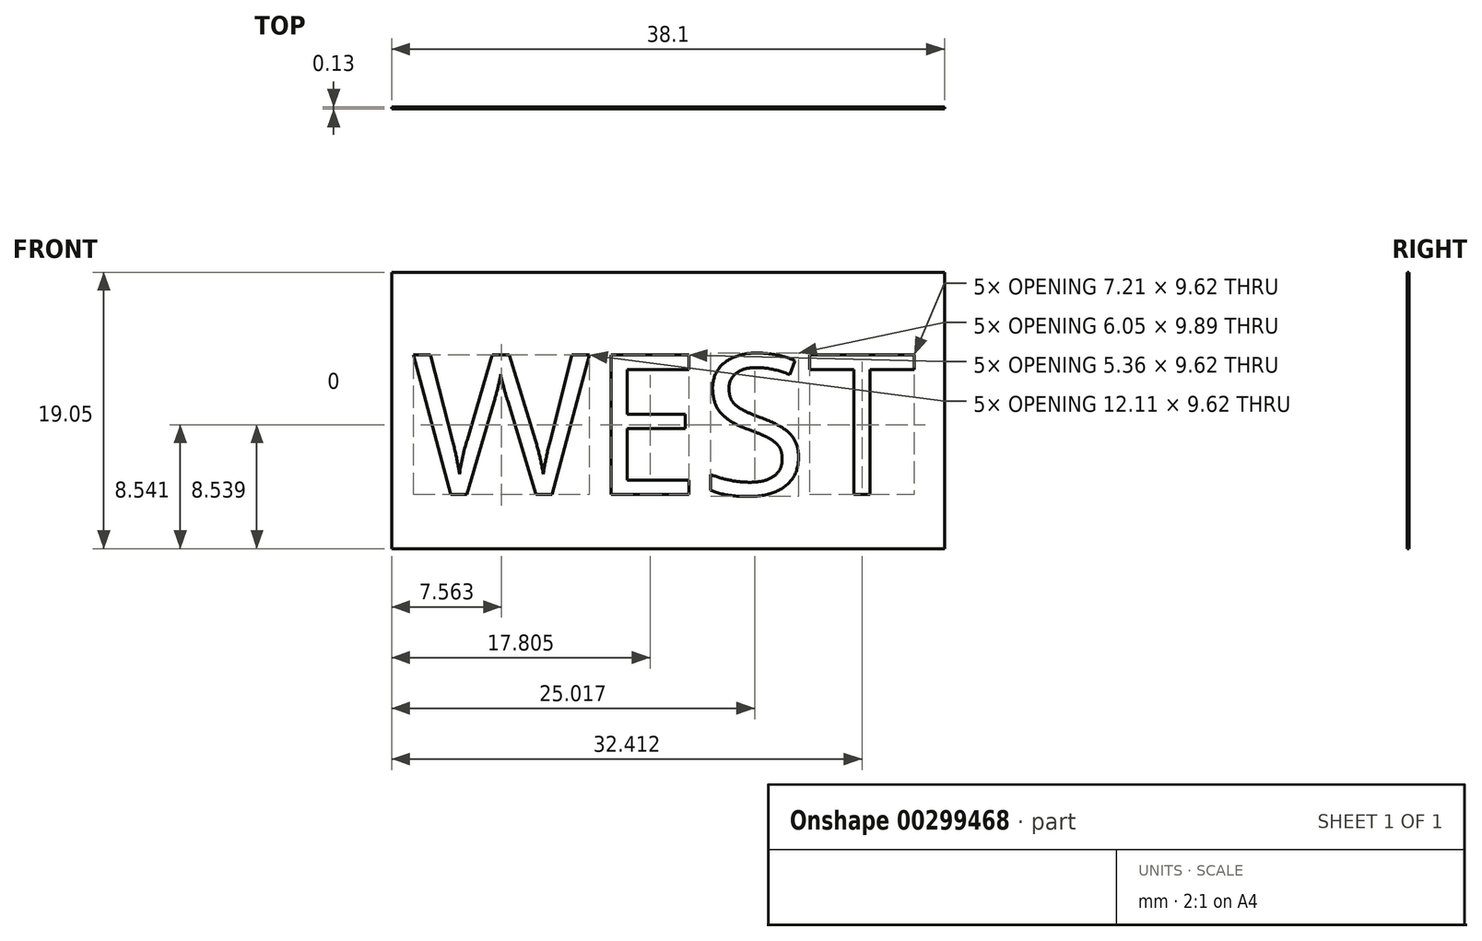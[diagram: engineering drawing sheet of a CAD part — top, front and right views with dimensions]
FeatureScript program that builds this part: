
annotation { "Feature Type Name" : "Feature", "Feature Type Description" : "" }
export const myFeature = defineFeature(function(context is Context, id is Id, definition is map)
    precondition{}
    {
        {
            var Q0;
            Q0=qCreatedBy(makeId("Front.planeOp"),FACE);
            var sketch = newSketch(context, id + "F0", { "sketchPlane" : qUnion([Q0])});
            skLineSegment(sketch, "E0.bottom", {"start": v(0, 0) * mm, "end": v(38.1, 0) * mm});
            skLineSegment(sketch, "E0.top", {"start": v(0, 19.05) * mm, "end": v(38.1, 19.05) * mm});
            skLineSegment(sketch, "E0.left", {"start": v(0, 0) * mm, "end": v(0, 19.05) * mm});
            skLineSegment(sketch, "E0.right", {"start": v(38.1, 0) * mm, "end": v(38.1, 19.05) * mm});
            skSolve(sketch);
        }
        {
            var Q0;
            Q0=makeQuery(id+"F0.imprint","IMPRINT",FACE,{"disambiguationData":[TD([[makeQuery(id+"F0.imprint","IMPRINT",EDGE,{"derivedFrom":sQuery(id+"F0.wireOp",EDGE,"E0.bottom")}),1.0]])]});
            extrude(context, id + "F1", {"entities" : qUnion([Q0]), "depth" : 0.13 * mm});
        }
        {
            var Q0;
            Q0=makeQuery(id+"F1.opExtrude","CAP_FACE",FACE,{"disambiguationData":[OSD([sQuery(id+"F0.wireOp",EDGE,"E0.bottom"),sQuery(id+"F0.wireOp",EDGE,"E0.top"),sQuery(id+"F0.wireOp",EDGE,"E0.left"),sQuery(id+"F0.wireOp",EDGE,"E0.right")])],"isStart":false});
            var sketch = newSketch(context, id + "F2", { "sketchPlane" : qUnion([Q0])});
            skText(sketch, "E1", { "text": "WEST", "fontName": "OpenSans-Regular.ttf"});
            const initialGuessF2  = {"E1": [0.00133, 0.00373, 1, 0, 0.0097]};
            skSetInitialGuess(sketch, initialGuessF2);
            skSolve(sketch);
        }
        {
            var Q0;
            Q0=qSketchRegion(id+"F2",true);
            extrude(context, id + "F3", {"entities" : qUnion([Q0]), "operationType" : NewBodyOperationType.REMOVE, "oppositeDirection" : true, "depth" : 0.05 * mm});
        }
    });
